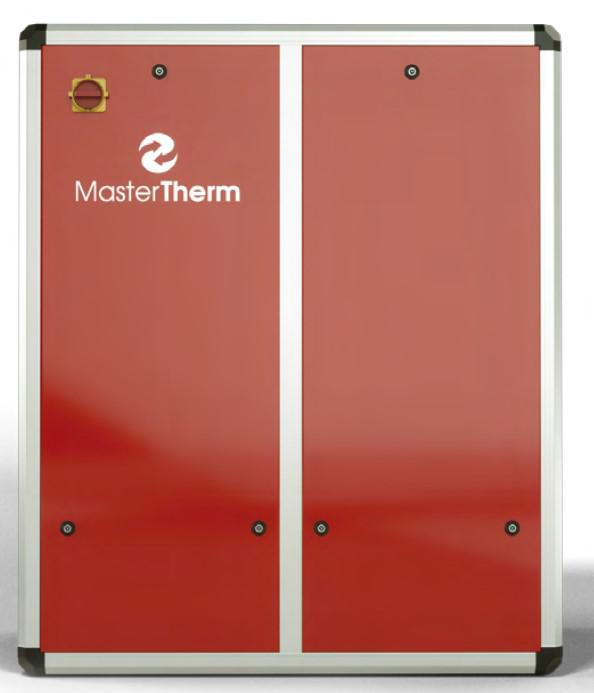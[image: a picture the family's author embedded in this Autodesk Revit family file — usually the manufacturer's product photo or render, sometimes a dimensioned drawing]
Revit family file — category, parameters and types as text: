
# Revit family: BoxAir-Inverter-P_ENG-RFA-2022
name_source: partatom
category: Mechanické zařízení
units: mm (PartAtom-declared; Revit-internal decimal feet)

## family parameters
Bod výpočtu místnosti = Ne
Kóta kulaté spojky = Použít průměr
Nadpis OmniClass = Climate Control (HVAC)
Ořezat dutým tvarem při načtení = Ne
Sdílené = Ne
Typ dílu = Normální
Vždy vertikální = Ano
Zachovat orientaci poznámky = Ne
Založené na pracovní rovině = Ne
Číslo OmniClass = 23.75.00.00

## types (4) — shared parameters
Drain = Ø40 mm
El. connection = 1xPG21; 1xPG29
Hot water – inlet = 1'' (OD)
Hot water – outlet = 1'' (OD)
MT_CI diameter = 28 mm  [stored 0.0918635 ft]
MT_CO diameter = 28 mm  [stored 0.0918635 ft]
MT_active power = 0 W
MT_angle offset = 60 mm  [stored 0.19685 ft]
MT_apparent power = 0 VA
MT_case mat = MT_RAL7016
MT_clearance back = 250 mm  [stored 0.82021 ft]
MT_clearance top = 200 mm  [stored 0.656168 ft]
MT_drain diameter = 40 mm  [stored 0.131234 ft]
MT_frequency (Hz) = 50 Hz
MT_ground height = 30 mm  [stored 0.0984252 ft]
MT_pipe mat = MT_angle-corner
Popis = Air-to-water heat pump (R290)
URL = https://www.mastertherm.eu
Výrobce = Master Therm
zero-valued in all types: Cena, MT_CosPhi, Výchozí výška

## per-type parameters (varying)
- BA22IP: Komentáře k typům=COMPRESSOR: BLDC Inverter; 25 – 120 rps; oil (PZ68S) – 0.3 l; max. op. current – 8 A; EVAPORATOR: Coil (Al/Cu); heat transfer area – 21 m2; fin spacing – 2.0 mm; max. overpress. – 4.2 MPa; max. air flow – 3000 m3/h; max. power in (fan) – 0.1 kW; fan diameter – 450 mm; speed (max.) – 700 1/min; LWA – 50 dB; defrost – reversal; CONDENSER: PHE; AISI316; water flow – 0.20 kg/s; min. flow – 0.10 kg/s; temp. difference – 5 K; water volume – 7.0 l; max. water overpress. – 250 kPa; max. refr. overpress. – 4.2 MPa; pump ext. head – 6.0 m; pump motor – 70 W; REFRIGERANT CIRCUIT: R290 (0.8 kg); PHE leak protection – 35% Propylene glycol; R290 leakage sensor – yes; AUX. HEATER: 5.7 + (2.8) kW; CONTROLS: controller – pCO5; EEV – yes; water probe – yes; SHW probe – yes; outdoor probe – yes; dynamic set point – yes; refrigerant probe – 2xPT; POWER SUPPLY: 1x230 (3x400) V; 50 Hz; max. current of compressor (aux. heater) – 16/(16)/(16) A; DIMENSIONS: hot water – 1" (OD); 90x130x53 cm; 120 kg; LIMITS: max. water overpress. – 0.25 MPa; max. refr. overpress. – 2.9 MPa; air min./max.: -20/+35 °C; water min./max.: 20/65 °C; MT_TYPE=22; MT_angle length_X=1184 mm  [stored 3.88451 ft]; MT_angle length_Y=406 mm  [stored 1.33202 ft]; MT_angle length_Z=765 mm  [stored 2.50984 ft]; MT_case depth=526 mm  [stored 1.72572 ft]; MT_case height=885 mm  [stored 2.90354 ft]; MT_case width=1304 mm  [stored 4.27822 ft]; MT_clearance front=1500 mm  [stored 4.92126 ft]; MT_clearance left=1500 mm  [stored 4.92126 ft]; MT_clearance right=1500 mm  [stored 4.92126 ft]; MT_cover front_X=1224 mm  [stored 4.01575 ft]; MT_cover front_Y=805 mm  [stored 2.64108 ft]; MT_cover front_Y-v2=-526 mm  [stored -1.72572 ft]; MT_cover side_X=446 mm  [stored 1.46325 ft]; MT_cover side_Y=805 mm  [stored 2.64108 ft]; MT_cover top_X=1224 mm  [stored 4.01575 ft]; MT_cover top_Y=446 mm  [stored 1.46325 ft]; MT_front grille H=805 mm  [stored 2.64108 ft]; MT_front grille W=726 mm  [stored 2.38189 ft]; MT_grille ext front Y=755 mm  [stored 2.47703 ft]; MT_max. current – compressor (A)=16 A; MT_max. currnet – aux. heater (A)=16 A; MT_side grille H=805 mm  [stored 2.64108 ft]; MT_side grille W=446 mm  [stored 1.46325 ft]; MT_voltage (V)=230 V; MT_weight (kg)=120; Model=BoxAir 22 Intverter P
- BA26IP: Komentáře k typům=COMPRESSOR: BLDC Inverter; 15 – 110 rps; oil (PZ68S) – 0.75 l; max. op. current – 21 A; EVAPORATOR: Coil (Al/Cu); heat transfer area – 21 m2; fin spacing – 2.0 mm; max. overpress. – 4.2 MPa; max. air flow – 3500 m3/h; max. power in (fan) – 0.1 kW; fan diameter – 450 mm; speed (max.) – 700 1/min; LWA – 53 dB; defrost – reversal; CONDENSER: PHE; AISI316; water flow – 0.27 kg/s; min. flow – 0.13 kg/s; temp. difference – 5 K; water volume – 7.0 l; max. water overpress. – 250 kPa; max. refr. overpress. – 4.2 MPa; pump ext. head – 6.0 m; pump motor – 70 W; REFRIGERANT CIRCUIT: R290 (0.9 kg); PHE leak protection – 35% Propylene glycol; R290 leakage sensor – yes; AUX. HEATER: 5.7 + (2.8) kW; CONTROLS: controller – pCO5; EEV – yes; water probe – yes; SHW probe – yes; outdoor probe – yes; dynamic set point – yes; refrigerant probe – 2xPT; POWER SUPPLY: 1x230 (3x400) V; 50 Hz; max. current of compressor (aux. heater) – 20/(16)/(16) A; DIMENSIONS: hot water – 1" (OD); 90x130x53 cm; 130 kg; LIMITS: max. water overpress. – 0.25 MPa; max. refr. overpress. – 2.9 MPa; air min./max.: -20/+35 °C; water min./max.: 20/65 °C; MT_TYPE=26; MT_angle length_X=1184 mm  [stored 3.88451 ft]; MT_angle length_Y=406 mm  [stored 1.33202 ft]; MT_angle length_Z=765 mm  [stored 2.50984 ft]; MT_case depth=526 mm  [stored 1.72572 ft]; MT_case height=885 mm  [stored 2.90354 ft]; MT_case width=1304 mm  [stored 4.27822 ft]; MT_clearance front=1500 mm  [stored 4.92126 ft]; MT_clearance left=1500 mm  [stored 4.92126 ft]; MT_clearance right=1500 mm  [stored 4.92126 ft]; MT_cover front_X=1224 mm  [stored 4.01575 ft]; MT_cover front_Y=805 mm  [stored 2.64108 ft]; MT_cover front_Y-v2=-526 mm  [stored -1.72572 ft]; MT_cover side_X=446 mm  [stored 1.46325 ft]; MT_cover side_Y=805 mm  [stored 2.64108 ft]; MT_cover top_X=1224 mm  [stored 4.01575 ft]; MT_cover top_Y=446 mm  [stored 1.46325 ft]; MT_front grille H=805 mm  [stored 2.64108 ft]; MT_front grille W=726 mm  [stored 2.38189 ft]; MT_grille ext front Y=755 mm  [stored 2.47703 ft]; MT_max. current – compressor (A)=20 A; MT_max. currnet – aux. heater (A)=16 A; MT_side grille H=805 mm  [stored 2.64108 ft]; MT_side grille W=446 mm  [stored 1.46325 ft]; MT_voltage (V)=230 V; MT_weight (kg)=130; Model=BoxAir 26 Intverter P
- BA37IP: Komentáře k typům=COMPRESSOR: BLDC Inverter; 15 – 100 rps; oil (PZ68S) – 0.9 l; max. op. current – 21 A; EVAPORATOR: Coil (Al/Cu); heat transfer area – 42 m2; fin spacing – 2.0 mm; max. overpress. – 3.0 MPa; max. air flow – 8000 m3/h; max. power in (fan) – 0.2 kW; fan diameter – 2x450 mm; speed (max.) – 700 1/min; LWA – 55 dB; defrost – reversal; CONDENSER: PHE; AISI316; water flow – 0.46 kg/s; min. flow – 0.23 kg/s; temp. difference – 5 K; water volume – 10.9 l; max. water overpress. – 250 kPa; max. refr. overpress. – 3.0 MPa; pump ext. head – 6.0 m; pump motor – 130 W; REFRIGERANT CIRCUIT: R290 (1.55 kg); PHE leak protection – 35% Propylene glycol; R290 leakage sensor – yes; AUX. HEATER: 7.5 + (7.5) kW; CONTROLS: controller – pCO5; EEV – yes; water probe – yes; SHW probe – yes; outdoor probe – yes; dynamic set point – yes; refrigerant probe – 2xPT; POWER SUPPLY: 3x400 V; 50 Hz; max. current of compressor (aux. heater) – 20 (25) A; DIMENSIONS: hot water – 1" (OD); 150x130x53 cm; 165 kg; LIMITS: max. water overpress. – 0.25 MPa; max. refr. overpress. – 2.9 MPa; air min./max.: -20/+35 °C; water min./max.: 20/65 °C; MT_TYPE=37; MT_angle length_X=1188 mm; MT_angle length_Y=408 mm; MT_angle length_Z=1378 mm  [stored 4.521 ft]; MT_case depth=528 mm  [stored 1.73228 ft]; MT_case height=1498 mm  [stored 4.9147 ft]; MT_case width=1308 mm; MT_clearance front=2000 mm  [stored 6.56168 ft]; MT_clearance left=2000 mm  [stored 6.56168 ft]; MT_clearance right=2000 mm  [stored 6.56168 ft]; MT_cover front_X=1228 mm; MT_cover front_Y=1418 mm  [stored 4.65223 ft]; MT_cover front_Y-v2=-528 mm  [stored -1.73228 ft]; MT_cover side_X=448 mm  [stored 1.46982 ft]; MT_cover side_Y=1418 mm  [stored 4.65223 ft]; MT_cover top_X=1228 mm; MT_cover top_Y=448 mm  [stored 1.46982 ft]; MT_front grille H=1418 mm  [stored 4.65223 ft]; MT_front grille W=730 mm; MT_grille ext front Y=1368 mm  [stored 4.48819 ft]; MT_max. current – compressor (A)=20 A; MT_max. currnet – aux. heater (A)=25 A; MT_side grille H=1418 mm  [stored 4.65223 ft]; MT_side grille W=448 mm  [stored 1.46982 ft]; MT_voltage (V)=400 V; MT_weight (kg)=165; Model=BoxAir 37 Intverter P
- BA45IP: Komentáře k typům=COMPRESSOR: BLDC Inverter; 15 – 90 rps; oil (HAF68D1U) – 2.0 l; max. op. current – 24 A; EVAPORATOR: Coil (Al/Cu); heat transfer area – 42 m2; fin spacing – 2.0 mm; max. overpress. – 3.0 MPa; max. air flow – 8000 m3/h; max. power in (fan) – 0.2 kW; fan diameter – 2x450 mm; speed (max.) – 700 1/min; LWA – 60 dB; defrost – reversal; CONDENSER: PHE; AISI316; water flow – 0.55 kg/s; min. flow – 0.27 kg/s; temp. difference – 5 K; water volume – 10.9 l; max. water overpress. – 250 kPa; max. refr. overpress. – 3.0 MPa; pump ext. head – 6.0 m; pump motor – 130 W; REFRIGERANT CIRCUIT: R290 (1.55 kg); PHE leak protection – 35% Propylene glycol; R290 leakage sensor – yes; AUX. HEATER: 7.5 + (7.5) kW; CONTROLS: controller – pCO5; EEV – yes; water probe – yes; SHW probe – yes; outdoor probe – yes; dynamic set point – yes; refrigerant probe – 2xPT; POWER SUPPLY: 3x400 V; 50 Hz; max. current of compressor (aux. heater) – 25 (32) A; DIMENSIONS: hot water – 1" (OD); 150x130x53 cm; 185 kg; LIMITS: max. water overpress. – 0.25 MPa; max. refr. overpress. – 2.9 MPa; air min./max.: -20/+35 °C; water min./max.: 20/65 °C; MT_TYPE=45; MT_angle length_X=1188 mm; MT_angle length_Y=408 mm; MT_angle length_Z=1378 mm  [stored 4.521 ft]; MT_case depth=528 mm  [stored 1.73228 ft]; MT_case height=1498 mm  [stored 4.9147 ft]; MT_case width=1308 mm; MT_clearance front=2000 mm  [stored 6.56168 ft]; MT_clearance left=2000 mm  [stored 6.56168 ft]; MT_clearance right=2000 mm  [stored 6.56168 ft]; MT_cover front_X=1228 mm; MT_cover front_Y=1418 mm  [stored 4.65223 ft]; MT_cover front_Y-v2=-528 mm  [stored -1.73228 ft]; MT_cover side_X=448 mm  [stored 1.46982 ft]; MT_cover side_Y=1418 mm  [stored 4.65223 ft]; MT_cover top_X=1228 mm; MT_cover top_Y=448 mm  [stored 1.46982 ft]; MT_front grille H=1418 mm  [stored 4.65223 ft]; MT_front grille W=730 mm; MT_grille ext front Y=1368 mm  [stored 4.48819 ft]; MT_max. current – compressor (A)=25 A; MT_max. currnet – aux. heater (A)=32 A; MT_side grille H=1418 mm  [stored 4.65223 ft]; MT_side grille W=448 mm  [stored 1.46982 ft]; MT_voltage (V)=400 V; MT_weight (kg)=185; Model=BoxAir 45 Intverter P

note: [stored X ft] marks values corroborated as IEEE doubles in the binary element streams (Revit-internal decimal feet)
